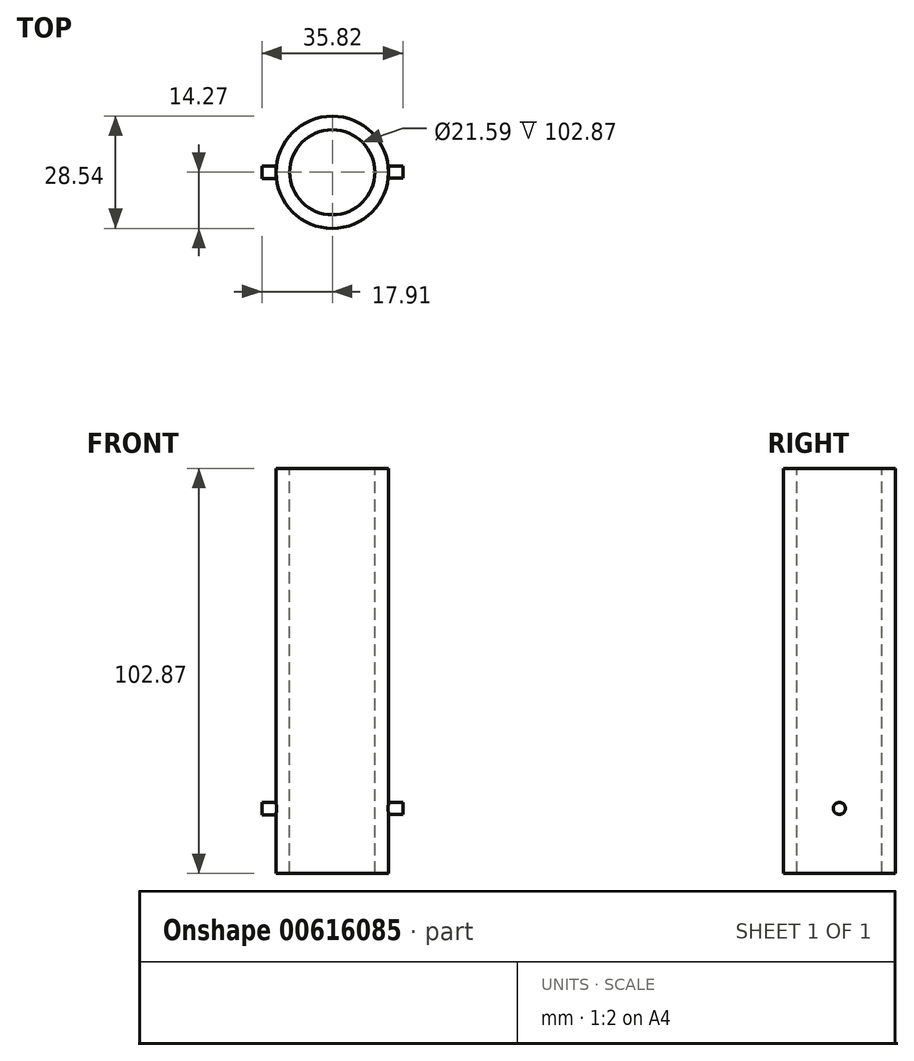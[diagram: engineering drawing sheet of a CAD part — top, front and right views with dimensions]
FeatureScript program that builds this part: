
annotation { "Feature Type Name" : "Feature", "Feature Type Description" : "" }
export const myFeature = defineFeature(function(context is Context, id is Id, definition is map)
    precondition{}
    {
        {
            var Q0;
            Q0=qCreatedBy(makeId("Top.planeOp"),FACE);
            var sketch = newSketch(context, id + "F0", { "sketchPlane" : qUnion([Q0])});
            skCircle(sketch, "E0", {"center": v(0, 0) * mm, "radius": 14.27 * mm});
            skCircle(sketch, "E1", {"center": v(0, 0) * mm, "radius": 12.83 * mm});
            skSolve(sketch);
        }
        {
            var Q0;
            Q0 = qSketchRegion(id + "F0", true);
            extrude(context, id + "F1", {"entities" : qUnion([Q0]), "depth" : 266.7 * mm, "offsetDistance" : 25.4 * mm});
        }
        {
            var Q0;
            Q0=makeQuery(id+"F1.opExtrude","CAP_FACE",FACE,{"disambiguationData":[OSD([sQuery(id+"F0.wireOp",EDGE,"E0"),sQuery(id+"F0.wireOp",EDGE,"E1")])],"isStart":false});
            var sketch = newSketch(context, id + "F2", { "sketchPlane" : qUnion([Q0])});
            skArc(sketch, "E2", {"start": v(-3.17, 13.92) * mm, "mid": v(0, -14.27) * mm, "end": v(3.18, 13.92) * mm});
            skArc(sketch, "E3", {"start": v(-3.18, 12.43) * mm, "mid": v(0, -12.83) * mm, "end": v(3.18, 12.43) * mm});
            skLineSegment(sketch, "E4", {"start": v(3.18, 13.92) * mm, "end": v(3.18, 12.43) * mm});
            skLineSegment(sketch, "E5", {"start": v(-3.18, 13.92) * mm, "end": v(-3.18, 12.43) * mm});
            skSolve(sketch);
        }
        {
            var Q0;
            Q0 = qSketchRegion(id + "F2", true);
            extrude(context, id + "F3", {"entities" : qUnion([Q0]), "operationType" : NewBodyOperationType.ADD, "depth" : 12.7 * mm, "offsetDistance" : 25.4 * mm});
        }
        {
            var Q0;
            Q0=makeQuery(id+"F3.opExtrude","CAP_FACE",FACE,{"disambiguationData":[OSD([sQuery(id+"F2.wireOp",EDGE,"E2"),sQuery(id+"F2.wireOp",EDGE,"E3"),sQuery(id+"F2.wireOp",EDGE,"E4"),sQuery(id+"F2.wireOp",EDGE,"E5")])],"isStart":false});
            var sketch = newSketch(context, id + "F4", { "sketchPlane" : qUnion([Q0])});
            skCircle(sketch, "E6", {"center": v(0, 0) * mm, "radius": 14.27 * mm});
            skCircle(sketch, "E7", {"center": v(0, 0) * mm, "radius": 12.83 * mm});
            skSolve(sketch);
        }
        {
            var Q0;
            Q0 = qSketchRegion(id + "F4", true);
            extrude(context, id + "F5", {"entities" : qUnion([Q0]), "operationType" : NewBodyOperationType.ADD, "depth" : 76.2 * mm, "offsetDistance" : 25.4 * mm});
        }
        {
            var Q0;
            Q0=qCreatedBy(makeId("Right.planeOp"),FACE);
            cPlane(context, id + "F6", {"entities" : qUnion([Q0]), "cplaneType" : CPlaneType.OFFSET, "offset" : 12.83 * mm, "width" : 152.4 * mm, "height" : 152.4 * mm});
        }
        {
            var Q0;
            Q0=qCreatedBy(id+"F6.planeOp",FACE);
            var sketch = newSketch(context, id + "F7", { "sketchPlane" : qUnion([Q0])});
            skCircle(sketch, "E8", {"center": v(0, 12.7) * mm, "radius": 1.52 * mm});
            skSolve(sketch);
        }
        {
            var Q0;
            Q0 = qSketchRegion(id + "F7", true);
            extrude(context, id + "F8", {"entities" : qUnion([Q0]), "operationType" : NewBodyOperationType.ADD, "depth" : 5.08 * mm, "offsetDistance" : 25.4 * mm});
        }
        {
            var Q0;
            Q0=qCreatedBy(makeId("Right.planeOp"),FACE);
            cPlane(context, id + "F9", {"entities" : qUnion([Q0]), "cplaneType" : CPlaneType.OFFSET, "offset" : 12.83 * mm, "oppositeDirection" : true, "width" : 152.4 * mm, "height" : 152.4 * mm});
        }
        {
            var Q0;
            Q0=qCreatedBy(id+"F9.planeOp",FACE);
            var sketch = newSketch(context, id + "F10", { "sketchPlane" : qUnion([Q0])});
            skCircle(sketch, "E9", {"center": v(0, 12.7) * mm, "radius": 1.59 * mm});
            skSolve(sketch);
        }
        {
            var Q0;
            Q0 = qSketchRegion(id + "F10", true);
            extrude(context, id + "F11", {"entities" : qUnion([Q0]), "operationType" : NewBodyOperationType.ADD, "oppositeDirection" : true, "depth" : 5.08 * mm, "offsetDistance" : 25.4 * mm});
        }
        {
            var Q0;
            Q0=makeQuery(id+"F5.opExtrude","CAP_FACE",FACE,{"disambiguationData":[OSD([sQuery(id+"F4.wireOp",EDGE,"E6"),sQuery(id+"F4.wireOp",EDGE,"E7")])],"isStart":false});
            var sketch = newSketch(context, id + "F12", { "sketchPlane" : qUnion([Q0])});
            skCircle(sketch, "E10", {"center": v(0, 0) * mm, "radius": 14.29 * mm});
            skSolve(sketch);
        }
        {
            var Q0;
            Q0 = qSketchRegion(id + "F12", true);
            extrude(context, id + "F13", {"entities" : qUnion([Q0]), "operationType" : NewBodyOperationType.REMOVE, "oppositeDirection" : true, "depth" : 256.54 * mm, "offsetDistance" : 25.4 * mm});
        }
        {
            var Q0;
            Q0=makeQuery(id+"F1.opExtrude","CAP_FACE",FACE,{"disambiguationData":[OSD([sQuery(id+"F0.wireOp",EDGE,"E0"),sQuery(id+"F0.wireOp",EDGE,"E1")])],"isStart":true});
            var sketch = newSketch(context, id + "F14", { "sketchPlane" : qUnion([Q0])});
            skCircle(sketch, "E11", {"center": v(0, 0) * mm, "radius": 14.27 * mm});
            skCircle(sketch, "E12", {"center": v(0, 0) * mm, "radius": 12.83 * mm});
            skSolve(sketch);
        }
        {
            var Q0;
            Q0 = qSketchRegion(id + "F14", true);
            extrude(context, id + "F15", {"entities" : qUnion([Q0]), "operationType" : NewBodyOperationType.ADD, "depth" : 3.8 * mm, "offsetDistance" : 25.4 * mm});
        }
        {
            var Q0;
            Q0=makeQuery(id+"F13.boolean.opBoolean","COPY",FACE,{"derivedFrom":makeQuery(id+"F13.opExtrude","CAP_FACE",FACE,{"disambiguationData":[OSD([sQuery(id+"F12.wireOp",EDGE,"E10")])],"isStart":false})});
            var sketch = newSketch(context, id + "F16", { "sketchPlane" : qUnion([Q0])});
            skCircle(sketch, "E13", {"center": v(0, 0) * mm, "radius": 10.8 * mm});
            skCircle(sketch, "E14", {"center": v(0, 0) * mm, "radius": 14.27 * mm});
            skSolve(sketch);
        }
        {
            var Q0;
            Q0 = qSketchRegion(id + "F16", true);
            extrude(context, id + "F17", {"entities" : qUnion([Q0]), "operationType" : NewBodyOperationType.ADD, "oppositeDirection" : true, "depth" : 102.87 * mm, "offsetDistance" : 25.4 * mm});
        }
    });
